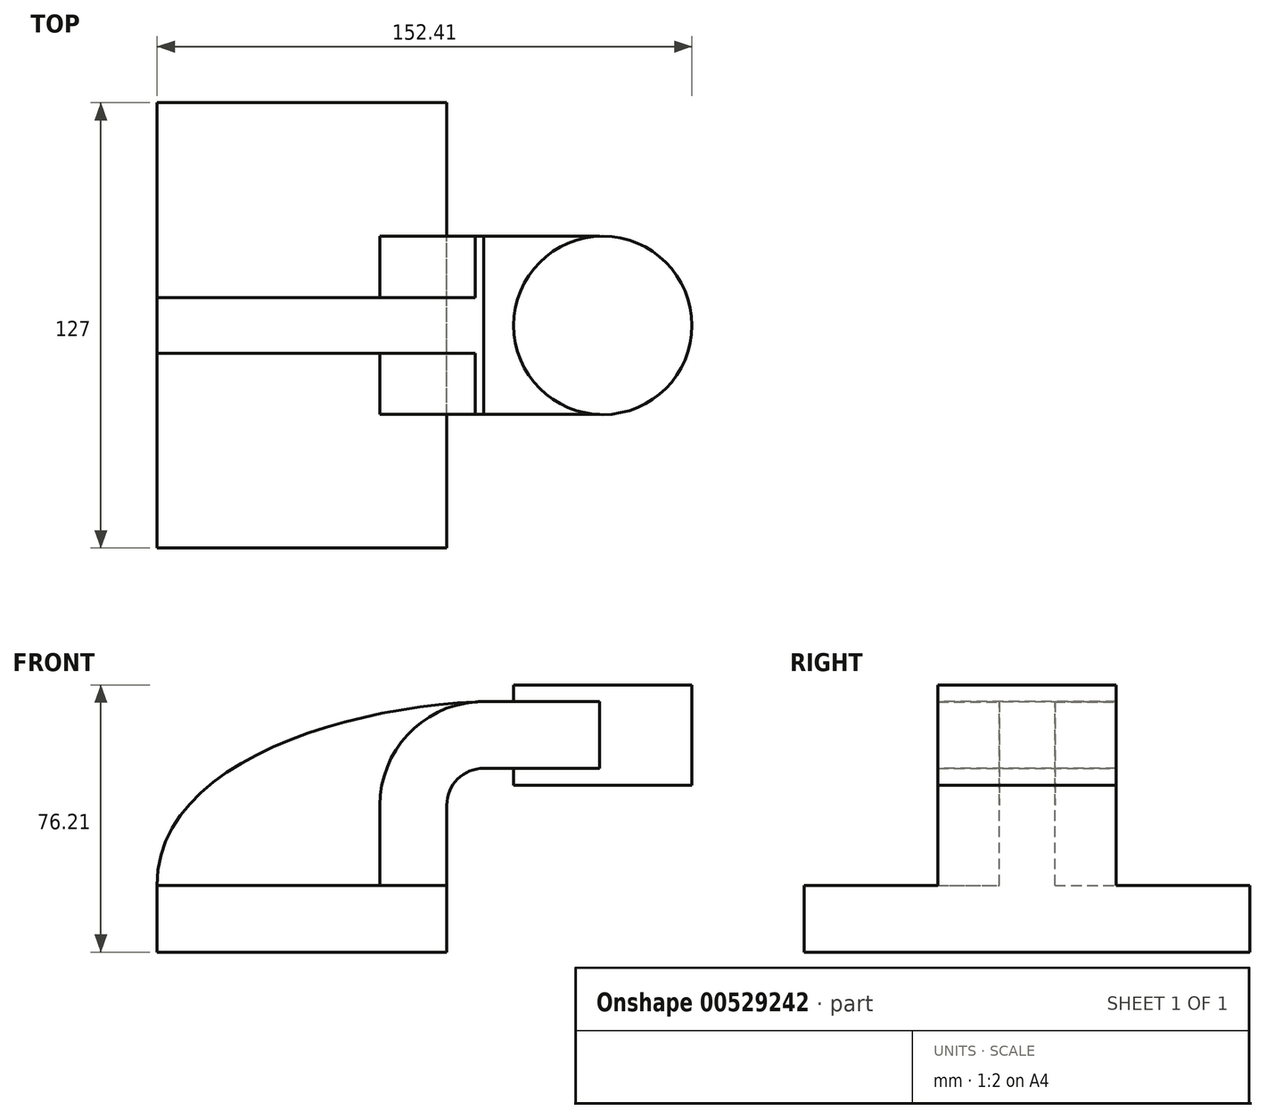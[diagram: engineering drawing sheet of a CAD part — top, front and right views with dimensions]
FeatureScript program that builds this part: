
annotation { "Feature Type Name" : "Feature", "Feature Type Description" : "" }
export const myFeature = defineFeature(function(context is Context, id is Id, definition is map)
    precondition{}
    {
        {
            var Q0;
            Q0=qCreatedBy(makeId("Front.planeOp"),FACE);
            var sketch = newSketch(context, id + "F0", { "sketchPlane" : qUnion([Q0])});
            skLineSegment(sketch, "E0.bottom", {"start": v(41.27, 9.53) * mm, "end": v(-41.28, 9.53) * mm});
            skLineSegment(sketch, "E0.top", {"start": v(41.28, -9.52) * mm, "end": v(-41.27, -9.52) * mm});
            skLineSegment(sketch, "E0.left", {"start": v(41.28, 9.53) * mm, "end": v(41.28, -9.52) * mm});
            skLineSegment(sketch, "E0.right", {"start": v(-41.28, 9.53) * mm, "end": v(-41.27, -9.52) * mm});
            skPoint(sketch, "E0.middle", {"position": v(0, 0) * mm});
            skLineSegment(sketch, "E1.bottom", {"start": v(111.12, 66.68) * mm, "end": v(60.33, 66.68) * mm});
            skLineSegment(sketch, "E1.top", {"start": v(111.12, 38.1) * mm, "end": v(60.33, 38.1) * mm});
            skLineSegment(sketch, "E1.left", {"start": v(111.12, 66.68) * mm, "end": v(111.12, 38.1) * mm});
            skLineSegment(sketch, "E1.right", {"start": v(60.33, 66.68) * mm, "end": v(60.33, 38.1) * mm});
            skPoint(sketch, "E1.middle", {"position": v(85.72, 52.39) * mm});
            skLineSegment(sketch, "E2", {"start": v(41.27, 9.53) * mm, "end": v(41.27, 32.36) * mm});
            skArc(sketch, "E3", {"start": v(41.27, 32.36) * mm, "mid": v(44.35, 39.8) * mm, "end": v(51.79, 42.88) * mm});
            skLineSegment(sketch, "E4", {"start": v(51.79, 42.88) * mm, "end": v(85.7, 42.88) * mm});
            skLineSegment(sketch, "E5.0", {"start": v(51.79, 61.93) * mm, "end": v(85.7, 61.93) * mm});
            skArc(sketch, "E5.1", {"start": v(22.23, 32.36) * mm, "mid": v(30.88, 53.27) * mm, "end": v(51.79, 61.93) * mm});
            skLineSegment(sketch, "E5.2", {"start": v(22.22, 9.53) * mm, "end": v(22.22, 32.36) * mm});
            skFitSpline(sketch, "E6", {"points": [v(-41.28, 9.53) * mm, v(51.79, 61.93) * mm], "startDerivative": vector(-0.95, 105.33) * mm, "endDerivative": vector(116.77, 3.9) * mm});
            skLineSegment(sketch, "E7", {"start": v(85.7, 61.93) * mm, "end": v(85.7, 42.88) * mm});
            skLineSegment(sketch, "E8", {"start": v(85.7, 66.68) * mm, "end": v(85.7, 38.1) * mm});
            skPoint(sketch, "E8.startSnap0", {"position": v(85.72, 66.68) * mm});
            skSolve(sketch);
        }
        {
            var Q0;
            Q0=makeQuery(id+"F0.imprint","IMPRINT",FACE,{"disambiguationData":[TD([[makeQuery(id+"F0.imprint","IMPRINT",EDGE,{"derivedFrom":sQuery(id+"F0.wireOp",EDGE,"E0.top")}),-1.0]])]});
            extrude(context, id + "F1", {"entities" : qUnion([Q0]), "endBound" : BoundingType.SYMMETRIC, "depth" : 127 * mm, "offsetDistance" : 25.4 * mm});
        }
        {
            var Q0;
            {var subQ1=sQuery(id+"F0.wireOp",EDGE,"E2");Q0=makeQuery(id+"F0.imprint","IMPRINT",FACE,{"disambiguationData":[TD([[makeQuery(id+"F0.imprint","IMPRINT",EDGE,{"derivedFrom":subQ1}),1.0]])]});}
            extrude(context, id + "F2", {"entities" : qUnion([Q0]), "operationType" : NewBodyOperationType.ADD, "endBound" : BoundingType.SYMMETRIC, "depth" : 50.8 * mm, "offsetDistance" : 25.4 * mm});
        }
        {
            var Q0;
            {var subQ0=sQuery(id+"F0.wireOp",EDGE,"E5.0");var subQ1=sQuery(id+"F0.wireOp",EDGE,"E1.right");var subQ2=makeQuery(id+"F0.imprint","INTERSECT",VERTEX,{"derivedFrom":[subQ1,subQ0]});Q0=makeQuery(id+"F0.imprint","IMPRINT",FACE,{"disambiguationData":[TD([[makeQuery(id+"F0.imprint","IMPRINT",EDGE,{"disambiguationData":[TD([[subQ2,-1.0]])],"derivedFrom":subQ1}),1.0]])]});}
            extrude(context, id + "F3", {"entities" : qUnion([Q0]), "operationType" : NewBodyOperationType.ADD, "endBound" : BoundingType.SYMMETRIC, "depth" : 50.8 * mm, "offsetDistance" : 25.4 * mm});
        }
        {
            var Q0;
            {var subQ4=sQuery(id+"F0.wireOp",EDGE,"E1.left");Q0=makeQuery(id+"F0.imprint","IMPRINT",FACE,{"disambiguationData":[TD([[makeQuery(id+"F0.imprint","IMPRINT",EDGE,{"derivedFrom":subQ4}),-1.0]])]});}
            var Q1;
            Q1=sQuery(id+"F0.wireOp",EDGE,"E8");
            revolve(context, id + "F4", {"operationType" : NewBodyOperationType.ADD, "entities" : qUnion([Q0]), "axis" : qUnion([Q1]), "revolveType" : RevolveType.FULL});
        }
        {
            var Q0;
            {var subQ3=sQuery(id+"F0.wireOp",EDGE,"E5.2");Q0=makeQuery(id+"F0.imprint","IMPRINT",FACE,{"disambiguationData":[TD([[makeQuery(id+"F0.imprint","IMPRINT",EDGE,{"derivedFrom":subQ3}),1.0]])]});}
            extrude(context, id + "F5", {"entities" : qUnion([Q0]), "operationType" : NewBodyOperationType.ADD, "endBound" : BoundingType.SYMMETRIC, "depth" : 15.88 * mm, "offsetDistance" : 25.4 * mm});
        }
    });
